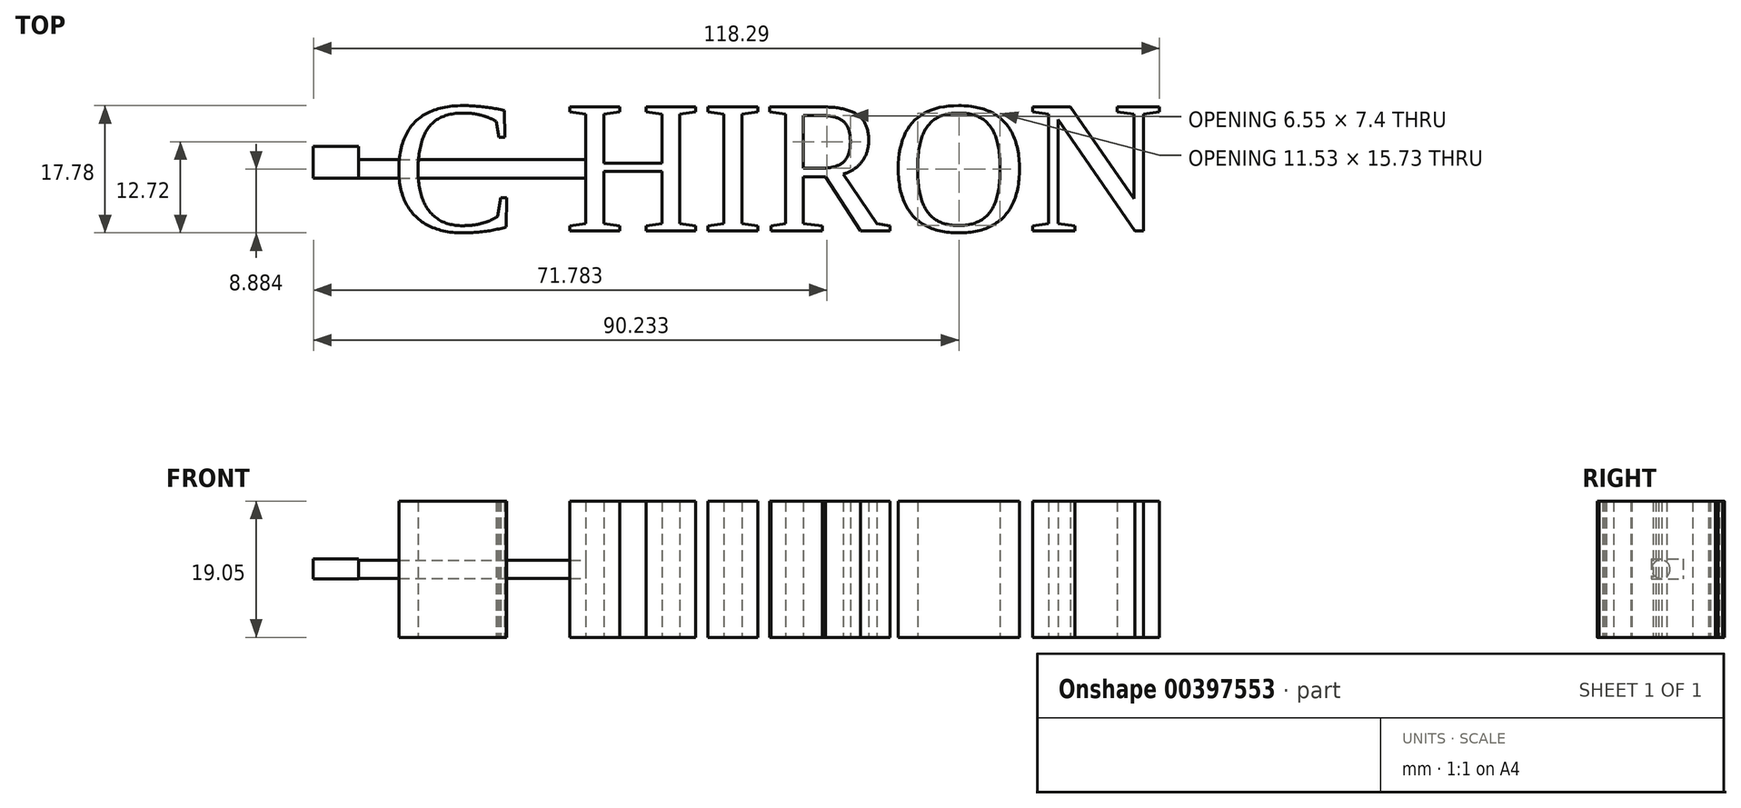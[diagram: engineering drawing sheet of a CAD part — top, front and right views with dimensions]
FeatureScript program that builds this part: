
annotation { "Feature Type Name" : "Feature", "Feature Type Description" : "" }
export const myFeature = defineFeature(function(context is Context, id is Id, definition is map)
    precondition{}
    {
        {
            var Q0;
            Q0=qCreatedBy(makeId("Top.planeOp"),FACE);
            var sketch = newSketch(context, id + "F0", { "sketchPlane" : qUnion([Q0])});
            skText(sketch, "E0", { "text": "C HIRON", "fontName": "Tinos-Regular.ttf"});
            const initialGuessF0  = {"E0": [0, 0, 1, 0, 0.01905]};
            skSetInitialGuess(sketch, initialGuessF0);
            skSolve(sketch);
        }
        {
            var Q0;
            Q0 = qSketchRegion(id + "F0", true);
            extrude(context, id + "F1", {"entities" : qUnion([Q0]), "depth" : 19.05 * mm});
        }
        {
            var Q0;
            Q0=makeQuery(id+"F1.opExtrude","SWEPT_FACE",FACE,{"disambiguationData":[OSD([sQuery(id+"F0.wireOp",EDGE,"E0.sketch_text.stroke-22")])]});
            var sketch = newSketch(context, id + "F2", { "sketchPlane" : qUnion([Q0])});
            skCircle(sketch, "E1", {"center": v(-8.67, 9.53) * mm, "radius": 1.29 * mm});
            skSolve(sketch);
        }
        {
            var Q0;
            Q0 = qSketchRegion(id + "F2", true);
            extrude(context, id + "F3", {"entities" : qUnion([Q0]), "depth" : 31.75 * mm});
        }
        {
            var Q0;
            Q0=makeQuery(id+"F3.opExtrude","CAP_FACE",FACE,{"disambiguationData":[OSD([sQuery(id+"F2.wireOp",EDGE,"E1")])],"isStart":false});
            var sketch = newSketch(context, id + "F4", { "sketchPlane" : qUnion([Q0])});
            skLineSegment(sketch, "E2.bottom", {"start": v(-7.35, 10.94) * mm, "end": v(-11.8, 10.94) * mm});
            skLineSegment(sketch, "E2.top", {"start": v(-7.35, 8.15) * mm, "end": v(-11.8, 8.15) * mm});
            skLineSegment(sketch, "E2.left", {"start": v(-7.35, 10.94) * mm, "end": v(-7.35, 8.15) * mm});
            skLineSegment(sketch, "E2.right", {"start": v(-11.8, 10.94) * mm, "end": v(-11.8, 8.15) * mm});
            skSolve(sketch);
        }
        {
            var Q0;
            Q0 = qSketchRegion(id + "F4", true);
            extrude(context, id + "F5", {"entities" : qUnion([Q0]), "depth" : 6.35 * mm, "offsetDistance" : 25.4 * mm});
        }
    });
